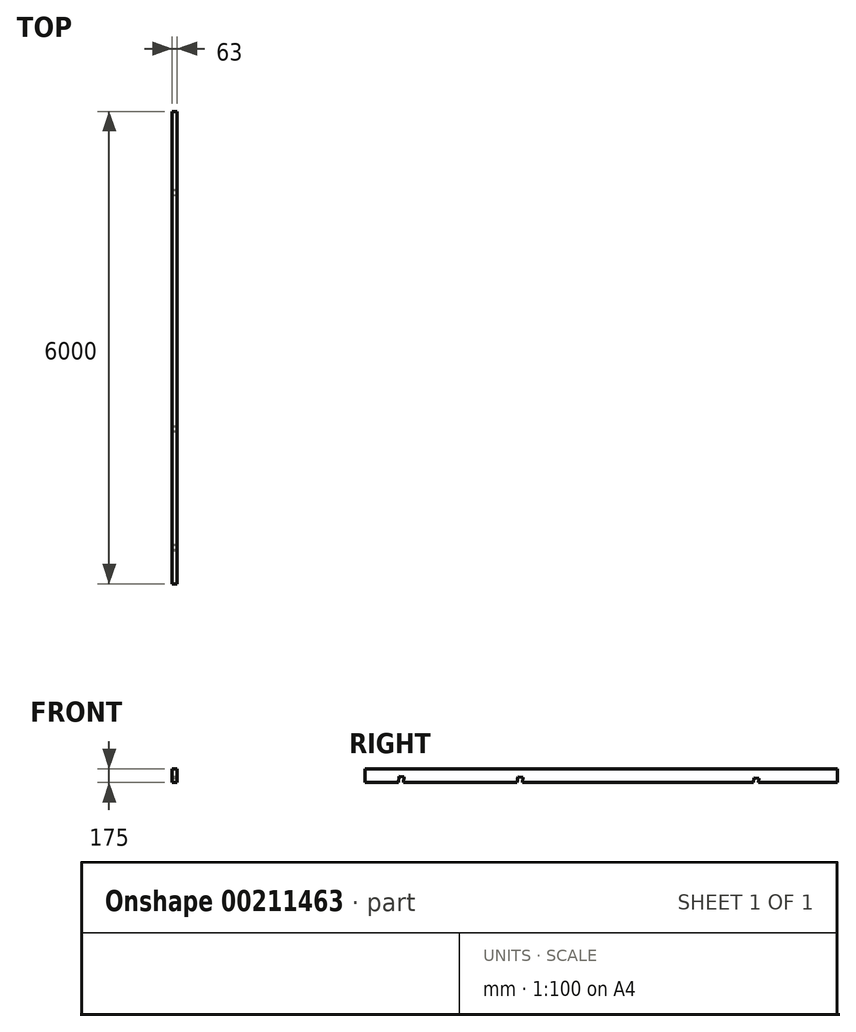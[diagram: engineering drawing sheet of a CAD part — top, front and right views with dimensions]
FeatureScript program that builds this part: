
annotation { "Feature Type Name" : "Feature", "Feature Type Description" : "" }
export const myFeature = defineFeature(function(context is Context, id is Id, definition is map)
    precondition{}
    {
        {
            var Q0;
            Q0=qCreatedBy(makeId("Front.planeOp"),FACE);
            var sketch = newSketch(context, id + "F0", { "sketchPlane" : qUnion([Q0])});
            skLineSegment(sketch, "E0.bottom", {"start": v(31.5, 87.5) * mm, "end": v(-31.5, 87.5) * mm});
            skLineSegment(sketch, "E0.top", {"start": v(31.5, -87.5) * mm, "end": v(-31.5, -87.5) * mm});
            skLineSegment(sketch, "E0.left", {"start": v(31.5, 87.5) * mm, "end": v(31.5, -87.5) * mm});
            skLineSegment(sketch, "E0.right", {"start": v(-31.5, 87.5) * mm, "end": v(-31.5, -87.5) * mm});
            skPoint(sketch, "E0.middle", {"position": v(0, 0) * mm});
            skSolve(sketch);
        }
        {
            var Q0;
            Q0=qSketchRegion(id+"F0",true);
            extrude(context, id + "F1", {"entities" : qUnion([Q0]), "depth" : 6000 * mm, "symmetric" : true});
        }
        {
            var Q0;
            Q0=makeQuery(id+"F1.opExtrude","SWEPT_FACE",FACE,{"disambiguationData":[OSD([sQuery(id+"F0.wireOp",EDGE,"E0.left")])]});
            var sketch = newSketch(context, id + "F2", { "sketchPlane" : qUnion([Q0])});
            skLineSegment(sketch, "E1", {"start": v(2000, -87.5) * mm, "end": v(2005.24, -37.5) * mm});
            skLineSegment(sketch, "E2", {"start": v(2005.24, -37.5) * mm, "end": v(1940.6, -30.72) * mm});
            skLineSegment(sketch, "E3", {"start": v(1940.6, -30.72) * mm, "end": v(1934.64, -87.5) * mm});
            skLineSegment(sketch, "E4", {"start": v(1934.64, -87.5) * mm, "end": v(2000, -87.5) * mm});
            skLineSegment(sketch, "E5", {"start": v(-1001.35, -87.5) * mm, "end": v(-994.77, -24.69) * mm});
            skLineSegment(sketch, "E6", {"start": v(-994.77, -24.69) * mm, "end": v(-1059.42, -17.91) * mm});
            skLineSegment(sketch, "E7", {"start": v(-1059.42, -17.91) * mm, "end": v(-1066.7, -87.5) * mm});
            skLineSegment(sketch, "E8", {"start": v(-1066.7, -87.5) * mm, "end": v(-1001.35, -87.5) * mm});
            skLineSegment(sketch, "E9", {"start": v(-2509.57, -87.5) * mm, "end": v(-2502.23, -17.5) * mm});
            skLineSegment(sketch, "E10", {"start": v(-2502.23, -17.5) * mm, "end": v(-2566.88, -10.72) * mm});
            skLineSegment(sketch, "E11", {"start": v(-2566.88, -10.72) * mm, "end": v(-2574.93, -87.5) * mm});
            skLineSegment(sketch, "E12", {"start": v(-2574.93, -87.5) * mm, "end": v(-2509.57, -87.5) * mm});
            skSolve(sketch);
        }
        {
            var Q0;
            Q0=qSketchRegion(id+"F2",true);
            extrude(context, id + "F3", {"entities" : qUnion([Q0]), "operationType" : NewBodyOperationType.REMOVE, "endBound" : BoundingType.UP_TO_NEXT, "oppositeDirection" : true, "depth" : 25 * mm});
        }
    });
